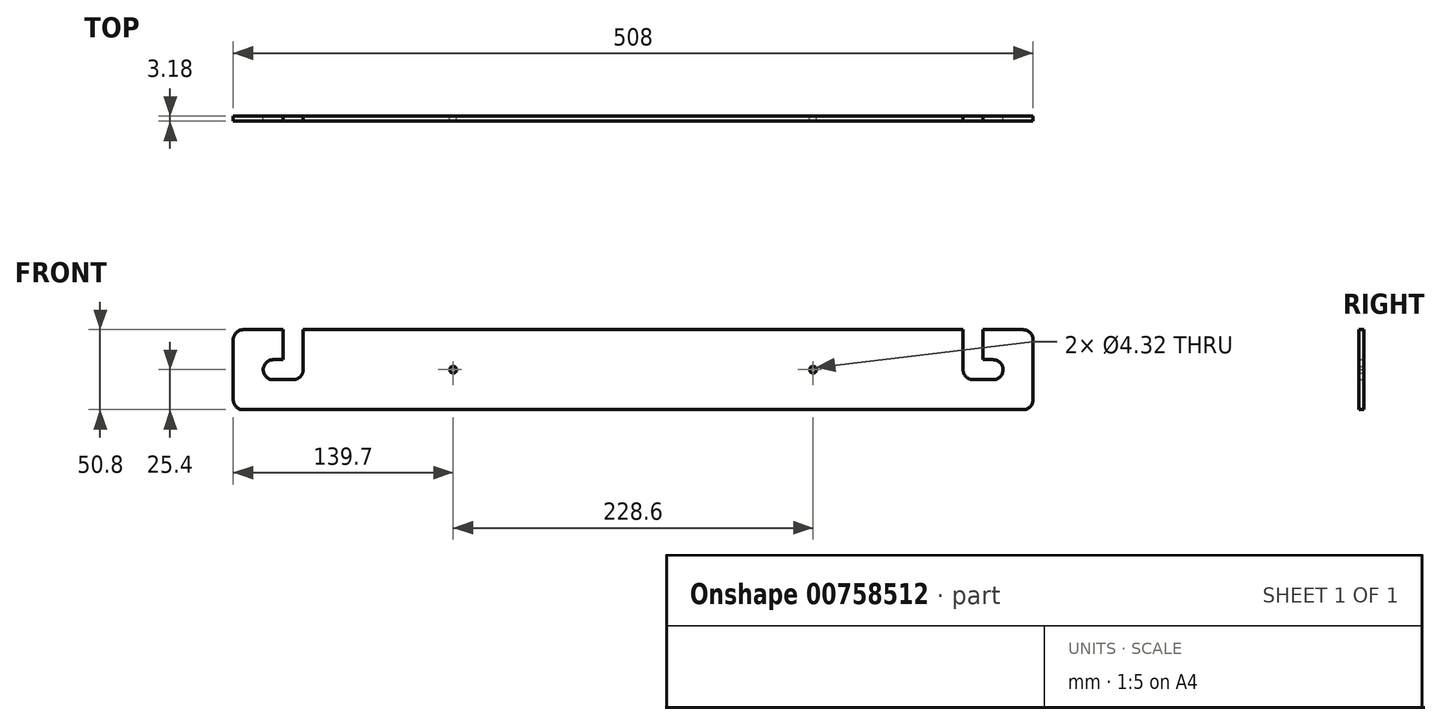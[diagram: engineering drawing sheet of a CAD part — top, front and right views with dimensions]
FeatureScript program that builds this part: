
annotation { "Feature Type Name" : "Feature", "Feature Type Description" : "" }
export const myFeature = defineFeature(function(context is Context, id is Id, definition is map)
    precondition{}
    {
        {
            var Q0;
            Q0=qCreatedBy(makeId("Front.planeOp"),FACE);
            var sketch = newSketch(context, id + "F0", { "sketchPlane" : qUnion([Q0])});
            skLineSegment(sketch, "E0.bottom", {"start": v(247.65, -25.4) * mm, "end": v(-247.65, -25.4) * mm});
            skLineSegment(sketch, "E0.top", {"start": v(247.65, 25.4) * mm, "end": v(222.25, 25.4) * mm});
            skLineSegment(sketch, "E0.left", {"start": v(254, -19.05) * mm, "end": v(254, 19.05) * mm});
            skLineSegment(sketch, "E0.right", {"start": v(-254, -19.05) * mm, "end": v(-254, 19.05) * mm});
            skPoint(sketch, "E0.middle", {"position": v(0, 0) * mm});
            skArc(sketch, "E1", {"start": v(-228.6, 6.35) * mm, "mid": v(-234.95, 0) * mm, "end": v(-228.6, -6.35) * mm});
            skPoint(sketch, "E1.centerSnap0", {"position": v(-254, 0) * mm});
            skArc(sketch, "E2", {"start": v(-215.9, -6.35) * mm, "mid": v(-211.37, -4.45) * mm, "end": v(-209.55, 0.11) * mm});
            skLineSegment(sketch, "E3", {"start": v(-209.55, 0.11) * mm, "end": v(-209.55, 25.4) * mm});
            skLineSegment(sketch, "E4", {"start": v(-228.6, 6.35) * mm, "end": v(-222.25, 6.35) * mm});
            skLineSegment(sketch, "E5", {"start": v(-228.6, -6.35) * mm, "end": v(-215.9, -6.35) * mm});
            skLineSegment(sketch, "E6", {"start": v(-222.25, 6.35) * mm, "end": v(-222.25, 25.4) * mm});
            skPoint(sketch, "E6.startSnap0", {"position": v(-222.25, 6.35) * mm});
            skPoint(sketch, "E7.orphan", {"position": v(-222.25, 0) * mm});
            skPoint(sketch, "E8.orphan", {"position": v(-215.9, 6.35) * mm});
            skLineSegment(sketch, "E9.MirrorCS", {"start": v(222.25, 6.35) * mm, "end": v(222.25, 25.4) * mm});
            skLineSegment(sketch, "E10.MirrorCS", {"start": v(209.55, 0.11) * mm, "end": v(209.55, 25.4) * mm});
            skArc(sketch, "E11.MirrorCS", {"start": v(215.9, -6.35) * mm, "mid": v(211.37, -4.45) * mm, "end": v(209.55, 0.11) * mm});
            skLineSegment(sketch, "E12.MirrorCS", {"start": v(228.6, -6.35) * mm, "end": v(215.9, -6.35) * mm});
            skArc(sketch, "E13.MirrorCS", {"start": v(228.6, 6.35) * mm, "mid": v(234.95, 0) * mm, "end": v(228.6, -6.35) * mm});
            skLineSegment(sketch, "E14.MirrorCS", {"start": v(228.6, 6.35) * mm, "end": v(222.25, 6.35) * mm});
            skLineSegment(sketch, "E15.trimOffspring", {"start": v(209.55, 25.4) * mm, "end": v(-209.55, 25.4) * mm});
            skLineSegment(sketch, "E16.trimOffspring", {"start": v(-222.25, 25.4) * mm, "end": v(-247.65, 25.4) * mm});
            skPoint(sketch, "E17.visualSharp", {"position": v(-254, 25.4) * mm});
            skArc(sketch, "E17.filletArc", {"start": v(-247.65, 25.4) * mm, "mid": v(-252.14, 23.54) * mm, "end": v(-254, 19.05) * mm});
            skPoint(sketch, "E18.visualSharp", {"position": v(-254, -25.4) * mm});
            skArc(sketch, "E18.filletArc", {"start": v(-254, -19.05) * mm, "mid": v(-252.14, -23.54) * mm, "end": v(-247.65, -25.4) * mm});
            skPoint(sketch, "E19.visualSharp", {"position": v(254, 25.4) * mm});
            skArc(sketch, "E19.filletArc", {"start": v(254, 19.05) * mm, "mid": v(252.14, 23.54) * mm, "end": v(247.65, 25.4) * mm});
            skPoint(sketch, "E20.visualSharp", {"position": v(254, -25.4) * mm});
            skArc(sketch, "E20.filletArc", {"start": v(247.65, -25.4) * mm, "mid": v(252.14, -23.54) * mm, "end": v(254, -19.05) * mm});
            skPoint(sketch, "E21.orphan", {"position": v(0, -25.4) * mm});
            skPoint(sketch, "E22.start.orphan", {"position": v(0, 25.4) * mm});
            skLineSegment(sketch, "E23", {"start": v(-152.4, 19.05) * mm, "end": v(-152.4, 3.18) * mm});
            skPoint(sketch, "E24", {"position": v(-152.4, -3.18) * mm});
            skPoint(sketch, "E25", {"position": v(-152.4, 3.17) * mm});
            skLineSegment(sketch, "E26.trimOffspring", {"start": v(-152.4, -3.18) * mm, "end": v(-152.4, -19.05) * mm});
            skLineSegment(sketch, "E27.MirrorCS", {"start": v(152.4, 19.05) * mm, "end": v(152.4, 3.18) * mm});
            skLineSegment(sketch, "E28.MirrorCS", {"start": v(152.4, -3.18) * mm, "end": v(152.4, -19.05) * mm});
            skCircle(sketch, "E29", {"center": v(-114.3, 0) * mm, "radius": 2.16 * mm});
            skCircle(sketch, "E30", {"center": v(114.3, 0) * mm, "radius": 2.16 * mm});
            skSolve(sketch);
        }
        {
            var Q0;
            Q0 = qSketchRegion(id + "F0", true);
            extrude(context, id + "F1", {"entities" : qUnion([Q0]), "depth" : 3.17 * mm, "offsetDistance" : 25.4 * mm});
        }
    });
